SOLIDWORKS PART (.sldprt)
format: sldprt  version: not decoded by parser v0  size: 234,496 bytes
history: native  units: mm
features: fillet x6, plane x4, material x1, sketch x1, extrude x1 (+9 scaffold rows collapsed)
feature tree (22):
  scaffold x9  (default folders/planes/origin — collapsed)
  material  "Materiał <nieokreślony>"
  plane  "Płaszczyzna przednia"
  plane  "Płaszczyzna górna"
  plane  "Płaszczyzna prawa"
  plane  "Płaszczyzna1"
  sketch  "Szkic1"
  extrude  "Dodanie-wyciągnięcie1"  Depth=600mm
  fillet  "Zaokrąglenie1"  Radius=20mm
  fillet  "Zaokrąglenie2"  Radius=20mm
  fillet  "Zaokrąglenie3"  Radius=20mm
  fillet  "Zaokrąglenie4"  Radius=20mm
  fillet  "Zaokrąglenie5"  Radius=20mm
  fillet  "Zaokrąglenie6"  Radius=20mm
decode coverage: 7 of 8 modeling features carry decoded parameters
note: suppression state not decoded; provenance and decode notes live in map.json
